SOLIDWORKS PART (.sldprt)
format: sldprt  version: not decoded by parser v0  size: 169,472 bytes
history: native  units: mm
features: sketch x6, plane x3, sweep x2, material x1, revolve x1, cut_extrude x1 (+8 scaffold rows collapsed)
feature tree (22):
  scaffold x8  (default folders/planes/origin — collapsed)
  material  "Matériau <non spécifié>"
  plane  "Face"
  plane  "Dessus"
  plane  "Droite"
  sketch  "Esquisse1"  dims[c1.D4=0.7mm c1.D1=12.0mm c1.D2=2.6mm c1.D3=1.5mm c1.D5=2.0mm c1.D6=~0.912594mm c2.D3=1.5mm c2.D4=0.7mm]
  revolve  "Révolution1"  Angle=360deg
  sketch  "Esquisse2"  dims[D1=3.5mm]
  cut_extrude  "Enlèv. mat.-Extru.1"  Depth=0.1mm
  sketch  "Esquisse3"  dims[D1=0.8mm D2=2.54mm]
  sketch  "Esquisse4"  dims[c1.D4=0.5mm c1.D1=1.5mm c1.D2=2.54mm c1.D3=2.0mm c2.D2=2.54mm]
  sweep  "Balayage2"
  sketch  "Esquisse6"  dims[D2=0.8mm D1=1.4mm]
  sketch  "Esquisse7"  dims[D4=0.5mm D1=1.5mm D2=2.54mm D3=2.0mm]
  sweep  "Balayage3"
decode coverage: 8 of 10 modeling features carry decoded parameters
note: ~ marks probable driven/reference dimensions
note: suppression state not decoded; provenance and decode notes live in map.json
